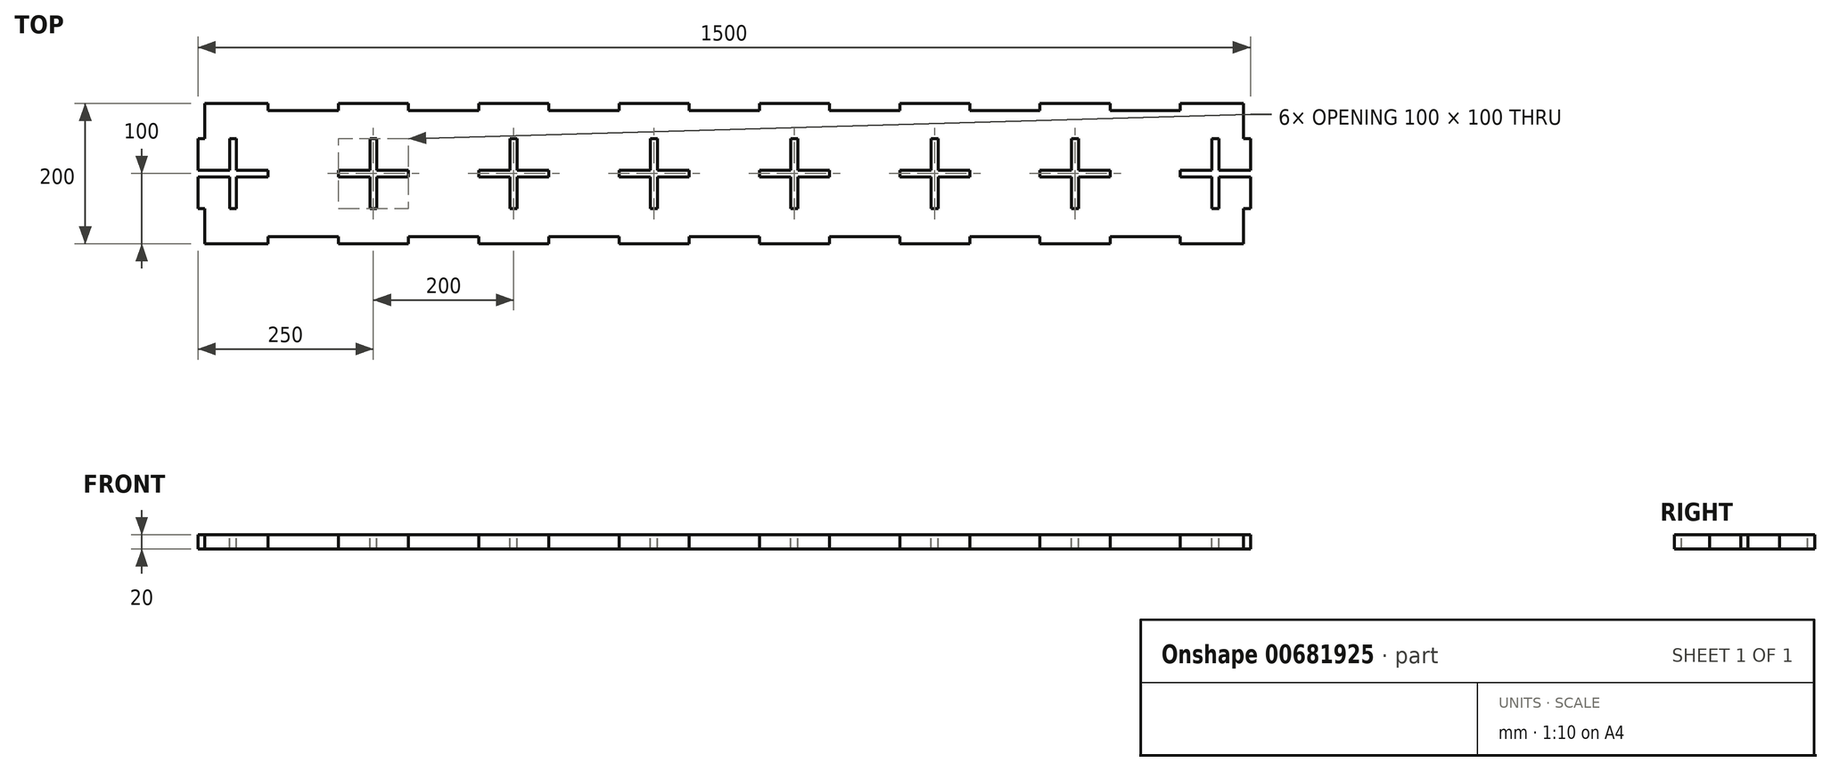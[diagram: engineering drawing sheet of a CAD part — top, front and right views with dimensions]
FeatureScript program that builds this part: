
annotation { "Feature Type Name" : "Feature", "Feature Type Description" : "" }
export const myFeature = defineFeature(function(context is Context, id is Id, definition is map)
    precondition{}
    {
        {
            var Q0;
            Q0=qCreatedBy(makeId("Top.planeOp"),FACE);
            var sketch = newSketch(context, id + "F0", { "sketchPlane" : qUnion([Q0])});
            skLineSegment(sketch, "E0.bottom", {"start": v(-750, 100) * mm, "end": v(750, 100) * mm});
            skLineSegment(sketch, "E0.top", {"start": v(-750, -100) * mm, "end": v(750, -100) * mm});
            skLineSegment(sketch, "E0.left", {"start": v(-750, 100) * mm, "end": v(-750, -100) * mm});
            skLineSegment(sketch, "E0.right", {"start": v(750, 100) * mm, "end": v(750, -100) * mm});
            skLineSegment(sketch, "E1", {"start": v(-921.86, 0) * mm, "end": v(985.96, 0) * mm, "construction": true});
            skLineSegment(sketch, "E2", {"start": v(0, 474.4) * mm, "end": v(0, -393.2) * mm, "construction": true});
            skSolve(sketch);
        }
        {
            var Q0;
            Q0=makeQuery(id+"F0.imprint","IMPRINT",FACE,{"disambiguationData":[TD([[makeQuery(id+"F0.imprint","IMPRINT",EDGE,{"derivedFrom":sQuery(id+"F0.wireOp",EDGE,"E0.bottom")}),-1.0]])]});
            extrude(context, id + "F1", {"entities" : qUnion([Q0]), "depth" : 20 * mm, "offsetDistance" : 25 * mm});
        }
        {
            var Q0;
            Q0=makeQuery(id+"F1.opExtrude","CAP_FACE",FACE,{"disambiguationData":[OSD([sQuery(id+"F0.wireOp",EDGE,"E0.bottom"),sQuery(id+"F0.wireOp",EDGE,"E0.top"),sQuery(id+"F0.wireOp",EDGE,"E0.left"),sQuery(id+"F0.wireOp",EDGE,"E0.right")])],"isStart":false});
            var sketch = newSketch(context, id + "F2", { "sketchPlane" : qUnion([Q0])});
            skLineSegment(sketch, "E3.bottom", {"start": v(-650, 100) * mm, "end": v(-550, 100) * mm});
            skLineSegment(sketch, "E3.top", {"start": v(-650, 90) * mm, "end": v(-550, 90) * mm});
            skLineSegment(sketch, "E3.left", {"start": v(-650, 100) * mm, "end": v(-650, 90) * mm});
            skLineSegment(sketch, "E3.right", {"start": v(-550, 100) * mm, "end": v(-550, 90) * mm});
            skLineSegment(sketch, "E4.0.1.0", {"start": v(-650, -90) * mm, "end": v(-550, -90) * mm});
            skLineSegment(sketch, "E4.0.1.1", {"start": v(-650, -100) * mm, "end": v(-550, -100) * mm});
            skLineSegment(sketch, "E4.0.1.2", {"start": v(-650, -90) * mm, "end": v(-650, -100) * mm});
            skLineSegment(sketch, "E4.0.1.3", {"start": v(-550, -90) * mm, "end": v(-550, -100) * mm});
            skLineSegment(sketch, "E4.1.0.0", {"start": v(-450, 100) * mm, "end": v(-350, 100) * mm});
            skLineSegment(sketch, "E4.1.0.1", {"start": v(-450, 90) * mm, "end": v(-350, 90) * mm});
            skLineSegment(sketch, "E4.1.0.2", {"start": v(-450, 100) * mm, "end": v(-450, 90) * mm});
            skLineSegment(sketch, "E4.1.0.3", {"start": v(-350, 100) * mm, "end": v(-350, 90) * mm});
            skLineSegment(sketch, "E4.1.1.0", {"start": v(-450, -90) * mm, "end": v(-350, -90) * mm});
            skLineSegment(sketch, "E4.1.1.1", {"start": v(-450, -100) * mm, "end": v(-350, -100) * mm});
            skLineSegment(sketch, "E4.1.1.2", {"start": v(-450, -90) * mm, "end": v(-450, -100) * mm});
            skLineSegment(sketch, "E4.1.1.3", {"start": v(-350, -90) * mm, "end": v(-350, -100) * mm});
            skLineSegment(sketch, "E4.2.0.0", {"start": v(-250, 100) * mm, "end": v(-150, 100) * mm});
            skLineSegment(sketch, "E4.2.0.1", {"start": v(-250, 90) * mm, "end": v(-150, 90) * mm});
            skLineSegment(sketch, "E4.2.0.2", {"start": v(-250, 100) * mm, "end": v(-250, 90) * mm});
            skLineSegment(sketch, "E4.2.0.3", {"start": v(-150, 100) * mm, "end": v(-150, 90) * mm});
            skLineSegment(sketch, "E4.2.1.0", {"start": v(-250, -90) * mm, "end": v(-150, -90) * mm});
            skLineSegment(sketch, "E4.2.1.1", {"start": v(-250, -100) * mm, "end": v(-150, -100) * mm});
            skLineSegment(sketch, "E4.2.1.2", {"start": v(-250, -90) * mm, "end": v(-250, -100) * mm});
            skLineSegment(sketch, "E4.2.1.3", {"start": v(-150, -90) * mm, "end": v(-150, -100) * mm});
            skLineSegment(sketch, "E4.3.0.0", {"start": v(-50, 100) * mm, "end": v(50, 100) * mm});
            skLineSegment(sketch, "E4.3.0.1", {"start": v(-50, 90) * mm, "end": v(50, 90) * mm});
            skLineSegment(sketch, "E4.3.0.2", {"start": v(-50, 100) * mm, "end": v(-50, 90) * mm});
            skLineSegment(sketch, "E4.3.0.3", {"start": v(50, 100) * mm, "end": v(50, 90) * mm});
            skLineSegment(sketch, "E4.3.1.0", {"start": v(-50, -90) * mm, "end": v(50, -90) * mm});
            skLineSegment(sketch, "E4.3.1.1", {"start": v(-50, -100) * mm, "end": v(50, -100) * mm});
            skLineSegment(sketch, "E4.3.1.2", {"start": v(-50, -90) * mm, "end": v(-50, -100) * mm});
            skLineSegment(sketch, "E4.3.1.3", {"start": v(50, -90) * mm, "end": v(50, -100) * mm});
            skLineSegment(sketch, "E4.4.0.0", {"start": v(150, 100) * mm, "end": v(250, 100) * mm});
            skLineSegment(sketch, "E4.4.0.1", {"start": v(150, 90) * mm, "end": v(250, 90) * mm});
            skLineSegment(sketch, "E4.4.0.2", {"start": v(150, 100) * mm, "end": v(150, 90) * mm});
            skLineSegment(sketch, "E4.4.0.3", {"start": v(250, 100) * mm, "end": v(250, 90) * mm});
            skLineSegment(sketch, "E4.4.1.0", {"start": v(150, -90) * mm, "end": v(250, -90) * mm});
            skLineSegment(sketch, "E4.4.1.1", {"start": v(150, -100) * mm, "end": v(250, -100) * mm});
            skLineSegment(sketch, "E4.4.1.2", {"start": v(150, -90) * mm, "end": v(150, -100) * mm});
            skLineSegment(sketch, "E4.4.1.3", {"start": v(250, -90) * mm, "end": v(250, -100) * mm});
            skLineSegment(sketch, "E4.direction1", {"start": v(-650, 90) * mm, "end": v(-450, 90) * mm, "construction": true});
            skLineSegment(sketch, "E4.direction2", {"start": v(-650, 90) * mm, "end": v(-650, -100) * mm, "construction": true});
            skLineSegment(sketch, "E5.0.5.0", {"start": v(350, 100) * mm, "end": v(450, 100) * mm});
            skLineSegment(sketch, "E5.3.5.0", {"start": v(350, 90) * mm, "end": v(450, 90) * mm});
            skLineSegment(sketch, "E5.6.5.0", {"start": v(350, 100) * mm, "end": v(350, 90) * mm});
            skLineSegment(sketch, "E5.9.5.0", {"start": v(450, 100) * mm, "end": v(450, 90) * mm});
            skLineSegment(sketch, "E5.0.5.1", {"start": v(350, -90) * mm, "end": v(450, -90) * mm});
            skLineSegment(sketch, "E5.3.5.1", {"start": v(350, -100) * mm, "end": v(450, -100) * mm});
            skLineSegment(sketch, "E5.6.5.1", {"start": v(350, -90) * mm, "end": v(350, -100) * mm});
            skLineSegment(sketch, "E5.9.5.1", {"start": v(450, -90) * mm, "end": v(450, -100) * mm});
            skLineSegment(sketch, "E5.0.6.0", {"start": v(550, 100) * mm, "end": v(650, 100) * mm});
            skLineSegment(sketch, "E5.3.6.0", {"start": v(550, 90) * mm, "end": v(650, 90) * mm});
            skLineSegment(sketch, "E5.6.6.0", {"start": v(550, 100) * mm, "end": v(550, 90) * mm});
            skLineSegment(sketch, "E5.9.6.0", {"start": v(650, 100) * mm, "end": v(650, 90) * mm});
            skLineSegment(sketch, "E5.0.6.1", {"start": v(550, -90) * mm, "end": v(650, -90) * mm});
            skLineSegment(sketch, "E5.3.6.1", {"start": v(550, -100) * mm, "end": v(650, -100) * mm});
            skLineSegment(sketch, "E5.6.6.1", {"start": v(550, -90) * mm, "end": v(550, -100) * mm});
            skLineSegment(sketch, "E5.9.6.1", {"start": v(650, -90) * mm, "end": v(650, -100) * mm});
            skSolve(sketch);
        }
        {
            var Q0;
            Q0 = qSketchRegion(id + "F2", true);
            extrude(context, id + "F3", {"entities" : qUnion([Q0]), "operationType" : NewBodyOperationType.REMOVE, "endBound" : BoundingType.THROUGH_ALL, "oppositeDirection" : true, "depth" : 25 * mm, "offsetDistance" : 25 * mm});
        }
        {
            var Q0;
            Q0=makeQuery(id+"F1.opExtrude","CAP_FACE",FACE,{"disambiguationData":[OSD([sQuery(id+"F0.wireOp",EDGE,"E0.bottom"),sQuery(id+"F0.wireOp",EDGE,"E0.top"),sQuery(id+"F0.wireOp",EDGE,"E0.left"),sQuery(id+"F0.wireOp",EDGE,"E0.right")])],"isStart":false});
            var sketch = newSketch(context, id + "F4", { "sketchPlane" : qUnion([Q0])});
            skLineSegment(sketch, "E6.bottom", {"start": v(-705, 50) * mm, "end": v(-695, 50) * mm});
            skLineSegment(sketch, "E6.top", {"start": v(-705, -50) * mm, "end": v(-695, -50) * mm});
            skLineSegment(sketch, "E6.left", {"start": v(-705, 50) * mm, "end": v(-705, 5) * mm});
            skLineSegment(sketch, "E6.right", {"start": v(-695, 50) * mm, "end": v(-695, 5) * mm});
            skLineSegment(sketch, "E7.bottom", {"start": v(-750, 5) * mm, "end": v(-705, 5) * mm});
            skLineSegment(sketch, "E7.top", {"start": v(-750, -5) * mm, "end": v(-705, -5) * mm});
            skLineSegment(sketch, "E7.left", {"start": v(-750, 5) * mm, "end": v(-750, -5) * mm});
            skLineSegment(sketch, "E7.right", {"start": v(-650, 5) * mm, "end": v(-650, -5) * mm});
            skLineSegment(sketch, "E8.trimOffspring", {"start": v(-705, -5) * mm, "end": v(-705, -50) * mm});
            skLineSegment(sketch, "E9.trimOffspring", {"start": v(-695, 5) * mm, "end": v(-650, 5) * mm});
            skLineSegment(sketch, "E10.trimOffspring", {"start": v(-695, -5) * mm, "end": v(-695, -50) * mm});
            skLineSegment(sketch, "E11.trimOffspring", {"start": v(-695, -5) * mm, "end": v(-650, -5) * mm});
            skLineSegment(sketch, "E12", {"start": v(-490.48, 0) * mm, "end": v(-874.63, 0) * mm, "construction": true});
            skLineSegment(sketch, "E13", {"start": v(-700, 50) * mm, "end": v(-700, -50) * mm, "construction": true});
            skLineSegment(sketch, "E14.1.0.0", {"start": v(-495, -5) * mm, "end": v(-450, -5) * mm});
            skLineSegment(sketch, "E14.1.0.1", {"start": v(-495, -5) * mm, "end": v(-495, -50) * mm});
            skLineSegment(sketch, "E14.1.0.2", {"start": v(-495, 5) * mm, "end": v(-450, 5) * mm});
            skLineSegment(sketch, "E14.1.0.3", {"start": v(-505, -5) * mm, "end": v(-505, -50) * mm});
            skLineSegment(sketch, "E14.1.0.4", {"start": v(-550, -5) * mm, "end": v(-505, -5) * mm});
            skLineSegment(sketch, "E14.1.0.5", {"start": v(-550, 5) * mm, "end": v(-505, 5) * mm});
            skLineSegment(sketch, "E14.1.0.6", {"start": v(-495, 50) * mm, "end": v(-495, 5) * mm});
            skLineSegment(sketch, "E14.1.0.7", {"start": v(-505, 50) * mm, "end": v(-505, 5) * mm});
            skLineSegment(sketch, "E14.1.0.8", {"start": v(-500, 50) * mm, "end": v(-500, -50) * mm, "construction": true});
            skLineSegment(sketch, "E14.1.0.9", {"start": v(-450, 5) * mm, "end": v(-450, -5) * mm});
            skLineSegment(sketch, "E14.1.0.10", {"start": v(-550, 5) * mm, "end": v(-550, -5) * mm});
            skLineSegment(sketch, "E14.1.0.11", {"start": v(-505, -50) * mm, "end": v(-495, -50) * mm});
            skLineSegment(sketch, "E14.1.0.12", {"start": v(-505, 50) * mm, "end": v(-495, 50) * mm});
            skLineSegment(sketch, "E14.2.0.0", {"start": v(-295, -5) * mm, "end": v(-250, -5) * mm});
            skLineSegment(sketch, "E14.2.0.1", {"start": v(-295, -5) * mm, "end": v(-295, -50) * mm});
            skLineSegment(sketch, "E14.2.0.2", {"start": v(-295, 5) * mm, "end": v(-250, 5) * mm});
            skLineSegment(sketch, "E14.2.0.3", {"start": v(-305, -5) * mm, "end": v(-305, -50) * mm});
            skLineSegment(sketch, "E14.2.0.4", {"start": v(-350, -5) * mm, "end": v(-305, -5) * mm});
            skLineSegment(sketch, "E14.2.0.5", {"start": v(-350, 5) * mm, "end": v(-305, 5) * mm});
            skLineSegment(sketch, "E14.2.0.6", {"start": v(-295, 50) * mm, "end": v(-295, 5) * mm});
            skLineSegment(sketch, "E14.2.0.7", {"start": v(-305, 50) * mm, "end": v(-305, 5) * mm});
            skLineSegment(sketch, "E14.2.0.8", {"start": v(-300, 50) * mm, "end": v(-300, -50) * mm, "construction": true});
            skLineSegment(sketch, "E14.2.0.9", {"start": v(-250, 5) * mm, "end": v(-250, -5) * mm});
            skLineSegment(sketch, "E14.2.0.10", {"start": v(-350, 5) * mm, "end": v(-350, -5) * mm});
            skLineSegment(sketch, "E14.2.0.11", {"start": v(-305, -50) * mm, "end": v(-295, -50) * mm});
            skLineSegment(sketch, "E14.2.0.12", {"start": v(-305, 50) * mm, "end": v(-295, 50) * mm});
            skLineSegment(sketch, "E14.3.0.0", {"start": v(-95, -5) * mm, "end": v(-50, -5) * mm});
            skLineSegment(sketch, "E14.3.0.1", {"start": v(-95, -5) * mm, "end": v(-95, -50) * mm});
            skLineSegment(sketch, "E14.3.0.2", {"start": v(-95, 5) * mm, "end": v(-50, 5) * mm});
            skLineSegment(sketch, "E14.3.0.3", {"start": v(-105, -5) * mm, "end": v(-105, -50) * mm});
            skLineSegment(sketch, "E14.3.0.4", {"start": v(-150, -5) * mm, "end": v(-105, -5) * mm});
            skLineSegment(sketch, "E14.3.0.5", {"start": v(-150, 5) * mm, "end": v(-105, 5) * mm});
            skLineSegment(sketch, "E14.3.0.6", {"start": v(-95, 50) * mm, "end": v(-95, 5) * mm});
            skLineSegment(sketch, "E14.3.0.7", {"start": v(-105, 50) * mm, "end": v(-105, 5) * mm});
            skLineSegment(sketch, "E14.3.0.8", {"start": v(-100, 50) * mm, "end": v(-100, -50) * mm, "construction": true});
            skLineSegment(sketch, "E14.3.0.9", {"start": v(-50, 5) * mm, "end": v(-50, -5) * mm});
            skLineSegment(sketch, "E14.3.0.10", {"start": v(-150, 5) * mm, "end": v(-150, -5) * mm});
            skLineSegment(sketch, "E14.3.0.11", {"start": v(-105, -50) * mm, "end": v(-95, -50) * mm});
            skLineSegment(sketch, "E14.3.0.12", {"start": v(-105, 50) * mm, "end": v(-95, 50) * mm});
            skLineSegment(sketch, "E14.4.0.0", {"start": v(105, -5) * mm, "end": v(150, -5) * mm});
            skLineSegment(sketch, "E14.4.0.1", {"start": v(105, -5) * mm, "end": v(105, -50) * mm});
            skLineSegment(sketch, "E14.4.0.2", {"start": v(105, 5) * mm, "end": v(150, 5) * mm});
            skLineSegment(sketch, "E14.4.0.3", {"start": v(95, -5) * mm, "end": v(95, -50) * mm});
            skLineSegment(sketch, "E14.4.0.4", {"start": v(50, -5) * mm, "end": v(95, -5) * mm});
            skLineSegment(sketch, "E14.4.0.5", {"start": v(50, 5) * mm, "end": v(95, 5) * mm});
            skLineSegment(sketch, "E14.4.0.6", {"start": v(105, 50) * mm, "end": v(105, 5) * mm});
            skLineSegment(sketch, "E14.4.0.7", {"start": v(95, 50) * mm, "end": v(95, 5) * mm});
            skLineSegment(sketch, "E14.4.0.8", {"start": v(100, 50) * mm, "end": v(100, -50) * mm, "construction": true});
            skLineSegment(sketch, "E14.4.0.9", {"start": v(150, 5) * mm, "end": v(150, -5) * mm});
            skLineSegment(sketch, "E14.4.0.10", {"start": v(50, 5) * mm, "end": v(50, -5) * mm});
            skLineSegment(sketch, "E14.4.0.11", {"start": v(95, -50) * mm, "end": v(105, -50) * mm});
            skLineSegment(sketch, "E14.4.0.12", {"start": v(95, 50) * mm, "end": v(105, 50) * mm});
            skLineSegment(sketch, "E14.5.0.0", {"start": v(305, -5) * mm, "end": v(350, -5) * mm});
            skLineSegment(sketch, "E14.5.0.1", {"start": v(305, -5) * mm, "end": v(305, -50) * mm});
            skLineSegment(sketch, "E14.5.0.2", {"start": v(305, 5) * mm, "end": v(350, 5) * mm});
            skLineSegment(sketch, "E14.5.0.3", {"start": v(295, -5) * mm, "end": v(295, -50) * mm});
            skLineSegment(sketch, "E14.5.0.4", {"start": v(250, -5) * mm, "end": v(295, -5) * mm});
            skLineSegment(sketch, "E14.5.0.5", {"start": v(250, 5) * mm, "end": v(295, 5) * mm});
            skLineSegment(sketch, "E14.5.0.6", {"start": v(305, 50) * mm, "end": v(305, 5) * mm});
            skLineSegment(sketch, "E14.5.0.7", {"start": v(295, 50) * mm, "end": v(295, 5) * mm});
            skLineSegment(sketch, "E14.5.0.8", {"start": v(300, 50) * mm, "end": v(300, -50) * mm, "construction": true});
            skLineSegment(sketch, "E14.5.0.9", {"start": v(350, 5) * mm, "end": v(350, -5) * mm});
            skLineSegment(sketch, "E14.5.0.10", {"start": v(250, 5) * mm, "end": v(250, -5) * mm});
            skLineSegment(sketch, "E14.5.0.11", {"start": v(295, -50) * mm, "end": v(305, -50) * mm});
            skLineSegment(sketch, "E14.5.0.12", {"start": v(295, 50) * mm, "end": v(305, 50) * mm});
            skLineSegment(sketch, "E14.direction1", {"start": v(-705, -50) * mm, "end": v(-505, -50) * mm, "construction": true});
            skLineSegment(sketch, "E15.0.6.0", {"start": v(505, -5) * mm, "end": v(550, -5) * mm});
            skLineSegment(sketch, "E15.3.6.0", {"start": v(505, -5) * mm, "end": v(505, -50) * mm});
            skLineSegment(sketch, "E15.6.6.0", {"start": v(505, 5) * mm, "end": v(550, 5) * mm});
            skLineSegment(sketch, "E15.9.6.0", {"start": v(495, -5) * mm, "end": v(495, -50) * mm});
            skLineSegment(sketch, "E15.12.6.0", {"start": v(450, -5) * mm, "end": v(495, -5) * mm});
            skLineSegment(sketch, "E15.15.6.0", {"start": v(450, 5) * mm, "end": v(495, 5) * mm});
            skLineSegment(sketch, "E15.18.6.0", {"start": v(505, 50) * mm, "end": v(505, 5) * mm});
            skLineSegment(sketch, "E15.21.6.0", {"start": v(495, 50) * mm, "end": v(495, 5) * mm});
            skLineSegment(sketch, "E15.24.6.0", {"start": v(500, 50) * mm, "end": v(500, -50) * mm, "construction": true});
            skLineSegment(sketch, "E15.27.6.0", {"start": v(550, 5) * mm, "end": v(550, -5) * mm});
            skLineSegment(sketch, "E15.30.6.0", {"start": v(450, 5) * mm, "end": v(450, -5) * mm});
            skLineSegment(sketch, "E15.33.6.0", {"start": v(495, -50) * mm, "end": v(505, -50) * mm});
            skLineSegment(sketch, "E15.36.6.0", {"start": v(495, 50) * mm, "end": v(505, 50) * mm});
            skLineSegment(sketch, "E15.0.7.0", {"start": v(705, -5) * mm, "end": v(750, -5) * mm});
            skLineSegment(sketch, "E15.3.7.0", {"start": v(705, -5) * mm, "end": v(705, -50) * mm});
            skLineSegment(sketch, "E15.6.7.0", {"start": v(705, 5) * mm, "end": v(750, 5) * mm});
            skLineSegment(sketch, "E15.9.7.0", {"start": v(695, -5) * mm, "end": v(695, -50) * mm});
            skLineSegment(sketch, "E15.12.7.0", {"start": v(650, -5) * mm, "end": v(695, -5) * mm});
            skLineSegment(sketch, "E15.15.7.0", {"start": v(650, 5) * mm, "end": v(695, 5) * mm});
            skLineSegment(sketch, "E15.18.7.0", {"start": v(705, 50) * mm, "end": v(705, 5) * mm});
            skLineSegment(sketch, "E15.21.7.0", {"start": v(695, 50) * mm, "end": v(695, 5) * mm});
            skLineSegment(sketch, "E15.24.7.0", {"start": v(700, 50) * mm, "end": v(700, -50) * mm, "construction": true});
            skLineSegment(sketch, "E15.27.7.0", {"start": v(750, 5) * mm, "end": v(750, -5) * mm});
            skLineSegment(sketch, "E15.30.7.0", {"start": v(650, 5) * mm, "end": v(650, -5) * mm});
            skLineSegment(sketch, "E15.33.7.0", {"start": v(695, -50) * mm, "end": v(705, -50) * mm});
            skLineSegment(sketch, "E15.36.7.0", {"start": v(695, 50) * mm, "end": v(705, 50) * mm});
            skSolve(sketch);
        }
        {
            var Q0;
            Q0 = qSketchRegion(id + "F4", true);
            extrude(context, id + "F5", {"entities" : qUnion([Q0]), "operationType" : NewBodyOperationType.REMOVE, "endBound" : BoundingType.THROUGH_ALL, "oppositeDirection" : true, "depth" : 25 * mm, "offsetDistance" : 25 * mm});
        }
        {
            var Q0;
            Q0=makeQuery(id+"F1.opExtrude","CAP_FACE",FACE,{"disambiguationData":[OSD([sQuery(id+"F0.wireOp",EDGE,"E0.bottom"),sQuery(id+"F0.wireOp",EDGE,"E0.top"),sQuery(id+"F0.wireOp",EDGE,"E0.left"),sQuery(id+"F0.wireOp",EDGE,"E0.right")])],"isStart":false});
            var sketch = newSketch(context, id + "F6", { "sketchPlane" : qUnion([Q0])});
            skLineSegment(sketch, "E16.bottom", {"start": v(-750, 100) * mm, "end": v(-740, 100) * mm});
            skLineSegment(sketch, "E16.top", {"start": v(-750, 50) * mm, "end": v(-740, 50) * mm});
            skLineSegment(sketch, "E16.left", {"start": v(-750, 100) * mm, "end": v(-750, 50) * mm});
            skLineSegment(sketch, "E16.right", {"start": v(-740, 100) * mm, "end": v(-740, 50) * mm});
            skLineSegment(sketch, "E17.bottom", {"start": v(-750, -100) * mm, "end": v(-740, -100) * mm});
            skLineSegment(sketch, "E17.top", {"start": v(-750, -50) * mm, "end": v(-740, -50) * mm});
            skLineSegment(sketch, "E17.left", {"start": v(-750, -100) * mm, "end": v(-750, -50) * mm});
            skLineSegment(sketch, "E17.right", {"start": v(-740, -100) * mm, "end": v(-740, -50) * mm});
            skLineSegment(sketch, "E18.bottom", {"start": v(750, 100) * mm, "end": v(740, 100) * mm});
            skLineSegment(sketch, "E18.top", {"start": v(750, 50) * mm, "end": v(740, 50) * mm});
            skLineSegment(sketch, "E18.left", {"start": v(750, 100) * mm, "end": v(750, 50) * mm});
            skLineSegment(sketch, "E18.right", {"start": v(740, 100) * mm, "end": v(740, 50) * mm});
            skLineSegment(sketch, "E19.bottom", {"start": v(750, -100) * mm, "end": v(740, -100) * mm});
            skLineSegment(sketch, "E19.top", {"start": v(750, -50) * mm, "end": v(740, -50) * mm});
            skLineSegment(sketch, "E19.left", {"start": v(750, -100) * mm, "end": v(750, -50) * mm});
            skLineSegment(sketch, "E19.right", {"start": v(740, -100) * mm, "end": v(740, -50) * mm});
            skSolve(sketch);
        }
        {
            var Q0;
            Q0 = qSketchRegion(id + "F6", true);
            extrude(context, id + "F7", {"entities" : qUnion([Q0]), "operationType" : NewBodyOperationType.REMOVE, "endBound" : BoundingType.THROUGH_ALL, "oppositeDirection" : true, "depth" : 25 * mm, "offsetDistance" : 25 * mm});
        }
    });
